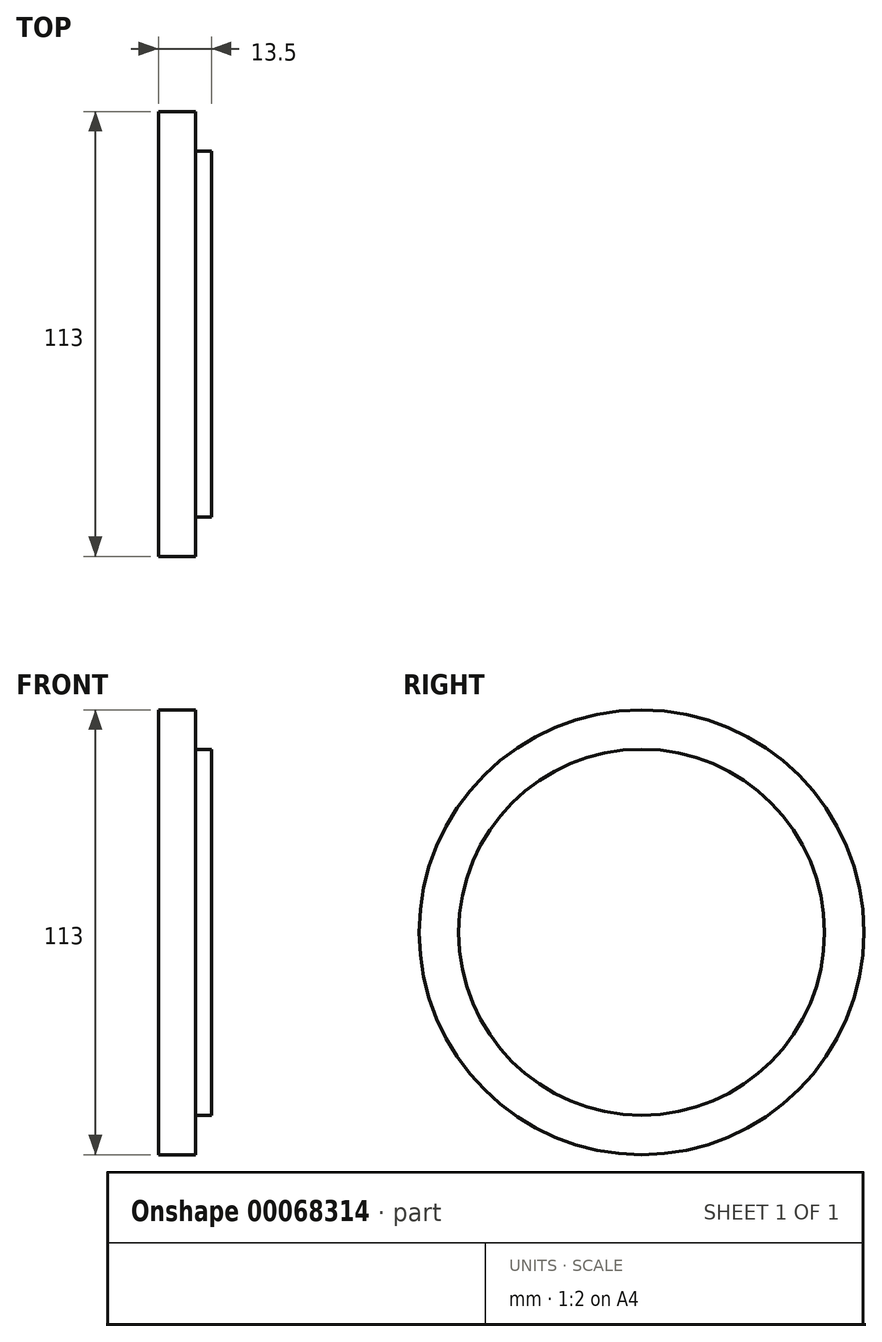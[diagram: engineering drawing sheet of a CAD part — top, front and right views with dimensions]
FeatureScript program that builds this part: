
annotation { "Feature Type Name" : "Feature", "Feature Type Description" : "" }
export const myFeature = defineFeature(function(context is Context, id is Id, definition is map)
    precondition{}
    {
        {
            var Q0;
            Q0=qCreatedBy(makeId("Right.planeOp"),FACE);
            var sketch = newSketch(context, id + "F0", { "sketchPlane" : qUnion([Q0])});
            skCircle(sketch, "E0", {"center": v(0, 0) * mm, "radius": 56.5 * mm});
            skSolve(sketch);
        }
        {
            var Q0;
            Q0=makeQuery(id+"F0.imprint","IMPRINT",FACE,{"disambiguationData":[TD([[makeQuery(id+"F0.imprint","IMPRINT",EDGE,{"derivedFrom":sQuery(id+"F0.wireOp",EDGE,"E0")}),1.0]])]});
            extrude(context, id + "F1", {"entities" : qUnion([Q0]), "depth" : 13.5 * mm});
        }
        {
            var Q0;
            Q0=qCreatedBy(makeId("Front.planeOp"),FACE);
            var sketch = newSketch(context, id + "F2", { "sketchPlane" : qUnion([Q0])});
            skLineSegment(sketch, "E1.bottom", {"start": v(9.5, 56.5) * mm, "end": v(13.5, 56.5) * mm});
            skLineSegment(sketch, "E1.top", {"start": v(9.5, 46.5) * mm, "end": v(13.5, 46.5) * mm});
            skLineSegment(sketch, "E1.left", {"start": v(9.5, 56.5) * mm, "end": v(9.5, 46.5) * mm});
            skLineSegment(sketch, "E1.right", {"start": v(13.5, 56.5) * mm, "end": v(13.5, 46.5) * mm});
            skSolve(sketch);
        }
        {
            var Q0;
            Q0 = qSketchRegion(id + "F2", true);
            var Q1;
            Q1=makeQuery(id+"F1.opExtrude","SWEPT_FACE",FACE,{"disambiguationData":[OSD([sQuery(id+"F0.wireOp",EDGE,"E0")])]});
            revolve(context, id + "F3", {"operationType" : NewBodyOperationType.REMOVE, "entities" : qUnion([Q0]), "axis" : qUnion([Q1]), "revolveType" : RevolveType.FULL, "oppositeDirection" : true});
        }
    });
